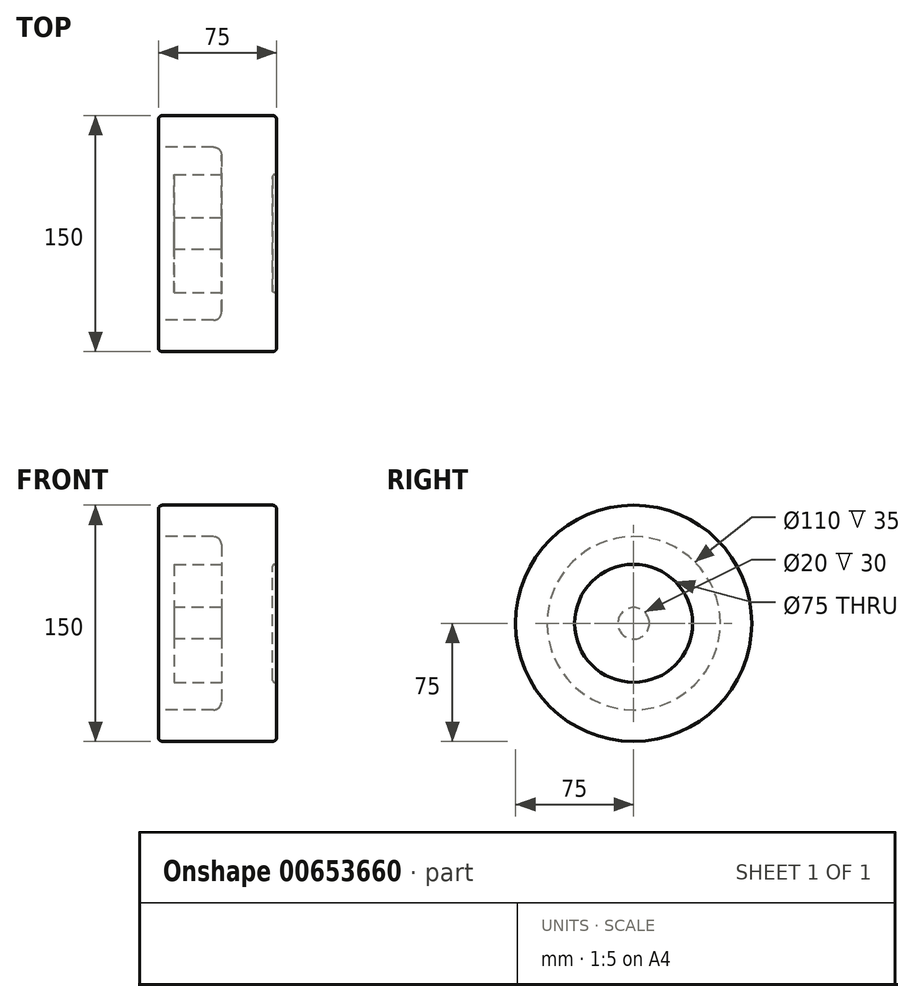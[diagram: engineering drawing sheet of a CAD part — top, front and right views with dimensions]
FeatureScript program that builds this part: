
annotation { "Feature Type Name" : "Feature", "Feature Type Description" : "" }
export const myFeature = defineFeature(function(context is Context, id is Id, definition is map)
    precondition{}
    {
        {
            var Q0;
            Q0=qCreatedBy(makeId("Right.planeOp"),FACE);
            var sketch = newSketch(context, id + "F0", { "sketchPlane" : qUnion([Q0])});
            skCircle(sketch, "E0", {"center": v(0, 0) * mm, "radius": 75 * mm});
            skSolve(sketch);
        }
        {
            var Q0;
            Q0 = qSketchRegion(id + "F0", true);
            extrude(context, id + "F1", {"entities" : qUnion([Q0]), "depth" : 75 * mm, "offsetDistance" : 25 * mm});
        }
        {
            var Q0;
            Q0=makeQuery(id+"F1.opExtrude","CAP_FACE",FACE,{"disambiguationData":[OSD([sQuery(id+"F0.wireOp",EDGE,"E0")])],"isStart":true});
            var sketch = newSketch(context, id + "F2", { "sketchPlane" : qUnion([Q0])});
            skCircle(sketch, "E1", {"center": v(0, 0) * mm, "radius": 55 * mm});
            skSolve(sketch);
        }
        {
            var Q0;
            Q0=makeQuery(id+"F2.imprint","IMPRINT",FACE,{"disambiguationData":[TD([[makeQuery(id+"F2.imprint","IMPRINT",EDGE,{"derivedFrom":sQuery(id+"F2.wireOp",EDGE,"E1")}),1.0]])]});
            extrude(context, id + "F3", {"entities" : qUnion([Q0]), "operationType" : NewBodyOperationType.REMOVE, "oppositeDirection" : true, "depth" : 40 * mm, "offsetDistance" : 25 * mm});
        }
        {
            var Q0;
            Q0=makeQuery(id+"F3.boolean.opBoolean","COPY",FACE,{"derivedFrom":makeQuery(id+"F3.opExtrude","CAP_FACE",FACE,{"disambiguationData":[OSD([sQuery(id+"F2.wireOp",EDGE,"E1")])],"isStart":false})});
            var sketch = newSketch(context, id + "F4", { "sketchPlane" : qUnion([Q0])});
            skCircle(sketch, "E2", {"center": v(0, 0) * mm, "radius": 37.5 * mm});
            skSolve(sketch);
        }
        {
            var Q0;
            Q0=makeQuery(id+"F4.imprint","IMPRINT",FACE,{"disambiguationData":[TD([[makeQuery(id+"F4.imprint","IMPRINT",EDGE,{"derivedFrom":sQuery(id+"F4.wireOp",EDGE,"E2")}),1.0]])]});
            extrude(context, id + "F5", {"entities" : qUnion([Q0]), "operationType" : NewBodyOperationType.ADD, "depth" : 30 * mm, "offsetDistance" : 25 * mm});
        }
        {
            var Q0;
            Q0=makeQuery(id+"F5.opExtrude","CAP_FACE",FACE,{"disambiguationData":[OSD([sQuery(id+"F4.wireOp",EDGE,"E2")])],"isStart":false});
            var sketch = newSketch(context, id + "F6", { "sketchPlane" : qUnion([Q0])});
            skCircle(sketch, "E3", {"center": v(0, 0) * mm, "radius": 10 * mm});
            skSolve(sketch);
        }
        {
            var Q0;
            Q0 = qSketchRegion(id + "F6", true);
            extrude(context, id + "F7", {"entities" : qUnion([Q0]), "operationType" : NewBodyOperationType.REMOVE, "oppositeDirection" : true, "depth" : 30 * mm, "offsetDistance" : 25 * mm});
        }
        {
            var Q0;
            Q0=makeQuery(id+"F5.opExtrude","CAP_EDGE",EDGE,{"disambiguationData":[OSD([sQuery(id+"F4.wireOp",EDGE,"E2")])],"isStart":true});
            var Q1;
            Q1=makeQuery(id+"F1.opExtrude","SWEPT_FACE",FACE,{"disambiguationData":[OSD([sQuery(id+"F0.wireOp",EDGE,"E0")])]});
            fillet(context, id + "F8", {"entities" : qUnion([Q0, Q1]), "radius" : 2.5 * mm, "tangentPropagation" : true, "allowEdgeOverflow" : false});
        }
        {
            var Q0;
            Q0=makeQuery(id+"F1.opExtrude","CAP_FACE",FACE,{"disambiguationData":[OSD([sQuery(id+"F0.wireOp",EDGE,"E0")])],"isStart":false});
            var sketch = newSketch(context, id + "F9", { "sketchPlane" : qUnion([Q0])});
            skCircle(sketch, "E4", {"center": v(0, 0) * mm, "radius": 37.5 * mm});
            skSolve(sketch);
        }
        {
            var Q0;
            Q0=makeQuery(id+"F9.imprint","IMPRINT",FACE,{"disambiguationData":[TD([[makeQuery(id+"F9.imprint","IMPRINT",EDGE,{"derivedFrom":sQuery(id+"F9.wireOp",EDGE,"E4")}),1.0]])]});
            extrude(context, id + "F10", {"entities" : qUnion([Q0]), "operationType" : NewBodyOperationType.REMOVE, "oppositeDirection" : true, "depth" : 2.5 * mm, "offsetDistance" : 25 * mm});
        }
        {
            var Q0;
            Q0=makeQuery(id+"F10.boolean.opBoolean","COPY",EDGE,{"derivedFrom":makeQuery(id+"F10.opExtrude","CAP_EDGE",EDGE,{"disambiguationData":[OSD([sQuery(id+"F9.wireOp",EDGE,"E4")])],"isStart":false})});
            var Q1;
            Q1=makeQuery(id+"F10.boolean.opBoolean","COPY",EDGE,{"derivedFrom":makeQuery(id+"F10.opExtrude","CAP_EDGE",EDGE,{"disambiguationData":[OSD([sQuery(id+"F9.wireOp",EDGE,"E4")])],"isStart":true})});
            fillet(context, id + "F11", {"entities" : qUnion([Q0, Q1]), "radius" : 1.25 * mm, "tangentPropagation" : true, "allowEdgeOverflow" : false});
        }
        {
            var Q0;
            Q0=makeQuery(id+"F3.boolean.opBoolean","COPY",EDGE,{"derivedFrom":makeQuery(id+"F3.opExtrude","CAP_EDGE",EDGE,{"disambiguationData":[OSD([sQuery(id+"F2.wireOp",EDGE,"E1")])],"isStart":false})});
            fillet(context, id + "F12", {"entities" : qUnion([Q0]), "radius" : 5 * mm, "tangentPropagation" : true, "allowEdgeOverflow" : false});
        }
    });
